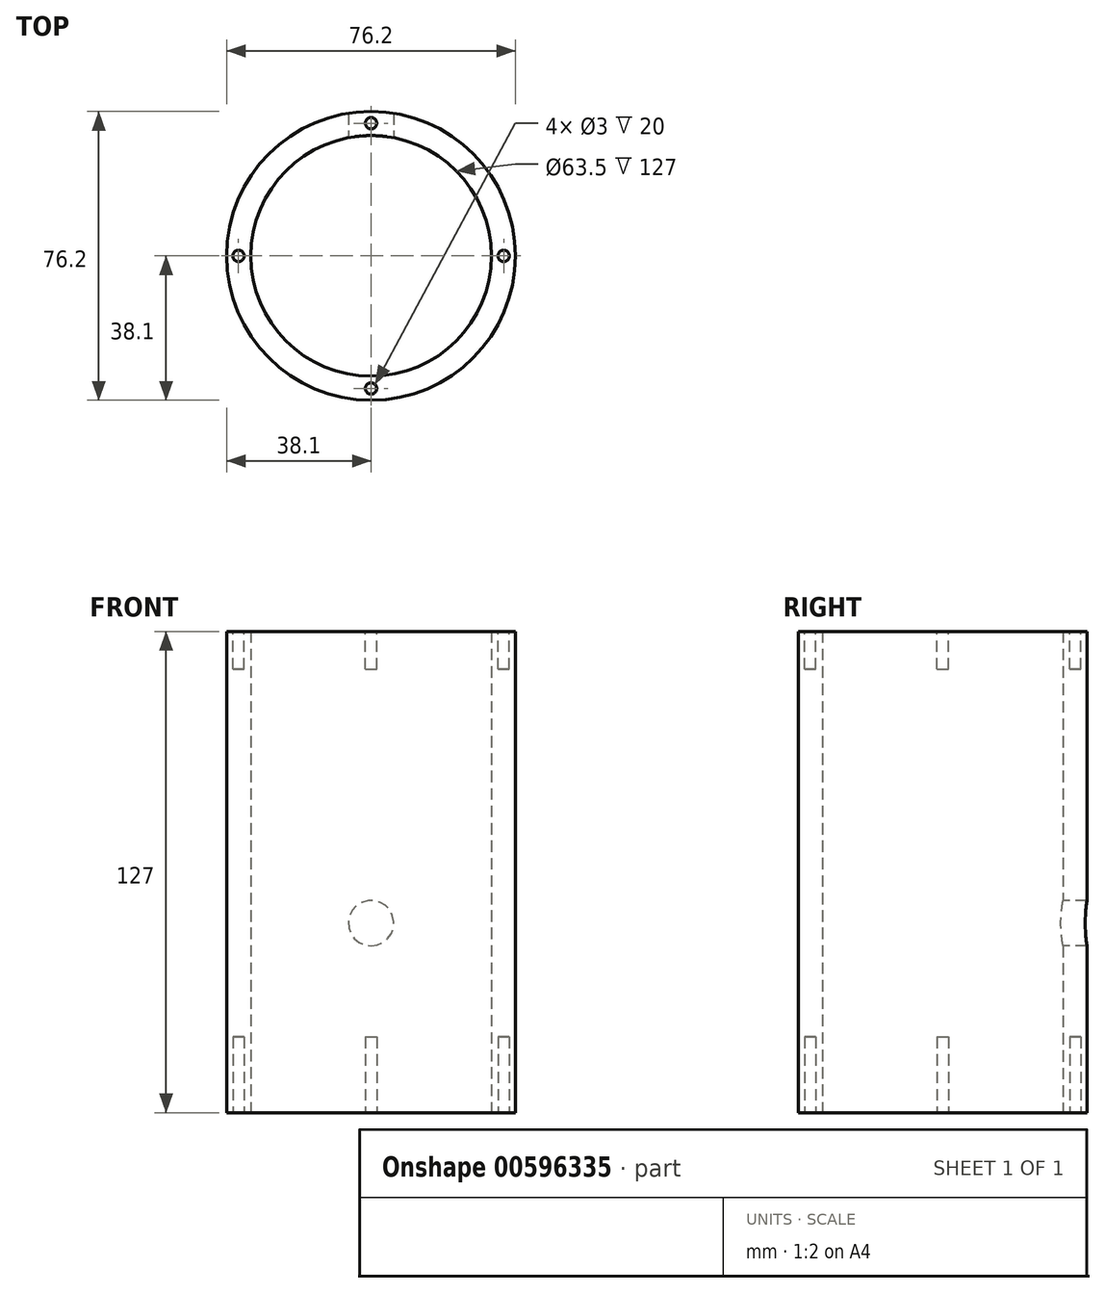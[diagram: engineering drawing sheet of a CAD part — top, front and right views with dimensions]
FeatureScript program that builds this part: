
annotation { "Feature Type Name" : "Feature", "Feature Type Description" : "" }
export const myFeature = defineFeature(function(context is Context, id is Id, definition is map)
    precondition{}
    {
        {
            var Q0;
            Q0=qCreatedBy(makeId("Top.planeOp"),FACE);
            var sketch = newSketch(context, id + "F0", { "sketchPlane" : qUnion([Q0])});
            skCircle(sketch, "E0", {"center": v(0, 0) * mm, "radius": 38.1 * mm});
            skCircle(sketch, "E1", {"center": v(0, 0) * mm, "radius": 31.75 * mm});
            skCircle(sketch, "E2", {"center": v(0, 0) * mm, "radius": 12.5 * mm});
            skCircle(sketch, "E3", {"center": v(0, -35) * mm, "radius": 1.5 * mm});
            skSolve(sketch);
        }
        {
            var Q0;
            Q0=makeQuery(id+"F0.imprint","IMPRINT",FACE,{"disambiguationData":[TD([[makeQuery(id+"F0.imprint","IMPRINT",EDGE,{"derivedFrom":sQuery(id+"F0.wireOp",EDGE,"E0")}),1.0]])]});
            var Q1;
            Q1=makeQuery(id+"F0.imprint","IMPRINT",FACE,{"disambiguationData":[TD([[makeQuery(id+"F0.imprint","IMPRINT",EDGE,{"derivedFrom":sQuery(id+"F0.wireOp",EDGE,"E3")}),1.0]])]});
            extrude(context, id + "F1", {"entities" : qUnion([Q0, Q1]), "depth" : 127 * mm, "offsetDistance" : 25 * mm});
        }
        {
            var Q0;
            Q0=qCreatedBy(makeId("Front.planeOp"),FACE);
            var sketch = newSketch(context, id + "F2", { "sketchPlane" : qUnion([Q0])});
            skCircle(sketch, "E4", {"center": v(0, 50) * mm, "radius": 6 * mm});
            skSolve(sketch);
        }
        {
            var Q0;
            Q0 = qSketchRegion(id + "F2", true);
            extrude(context, id + "F3", {"entities" : qUnion([Q0]), "operationType" : NewBodyOperationType.REMOVE, "oppositeDirection" : true, "depth" : 42.2 * mm, "offsetDistance" : 25 * mm});
        }
        {
            var Q0;
            Q0=makeQuery(id+"F1.opExtrude","CAP_FACE",FACE,{"disambiguationData":[OSD([sQuery(id+"F0.wireOp",EDGE,"E0"),sQuery(id+"F0.wireOp",EDGE,"E1")])],"isStart":false});
            var sketch = newSketch(context, id + "F4", { "sketchPlane" : qUnion([Q0])});
            skCircle(sketch, "E5", {"center": v(0, 35) * mm, "radius": 1.5 * mm});
            skSolve(sketch);
        }
        {
            var Q0;
            Q0=makeQuery(id+"F4.imprint","IMPRINT",FACE,{"disambiguationData":[TD([[makeQuery(id+"F4.imprint","IMPRINT",EDGE,{"derivedFrom":sQuery(id+"F4.wireOp",EDGE,"E5")}),1.0]])]});
            extrude(context, id + "F5", {"entities" : qUnion([Q0]), "oppositeDirection" : true, "depth" : 10 * mm, "offsetDistance" : 25 * mm});
        }
        {
            var Q0;
            Q0=makeQuery(id+"F5.opExtrude","SWEPT_BODY",BODY,{"disambiguationData":[OSD([sQuery(id+"F4.wireOp",EDGE,"E5")])]});
            var Q1;
            Q1=makeQuery(id+"F1.opExtrude","CAP_EDGE",EDGE,{"disambiguationData":[OSD([sQuery(id+"F0.wireOp",EDGE,"E0")])],"isStart":false});
            circularPattern(context, id + "F6", {"operationType" : NewBodyOperationType.REMOVE, "entities" : qUnion([Q0]), "axis" : qUnion([Q1]), "angle" : 360 * degree, "instanceCount" : 4, "equalSpace" : true});
        }
        {
            var Q0;
            Q0=makeQuery(id+"F0.imprint","IMPRINT",FACE,{"disambiguationData":[TD([[makeQuery(id+"F0.imprint","IMPRINT",EDGE,{"derivedFrom":sQuery(id+"F0.wireOp",EDGE,"E3")}),1.0]])]});
            extrude(context, id + "F7", {"entities" : qUnion([Q0]), "depth" : 20 * mm, "offsetDistance" : 25 * mm});
        }
        {
            var Q0;
            Q0=makeQuery(id+"F7.opExtrude","SWEPT_BODY",BODY,{"disambiguationData":[OSD([sQuery(id+"F0.wireOp",EDGE,"E3")])]});
            var Q1;
            Q1=sQuery(id+"F0.wireOp",EDGE,"E1");
            circularPattern(context, id + "F8", {"operationType" : NewBodyOperationType.REMOVE, "entities" : qUnion([Q0]), "axis" : qUnion([Q1]), "angle" : 360 * degree, "instanceCount" : 4, "equalSpace" : true});
        }
    });
